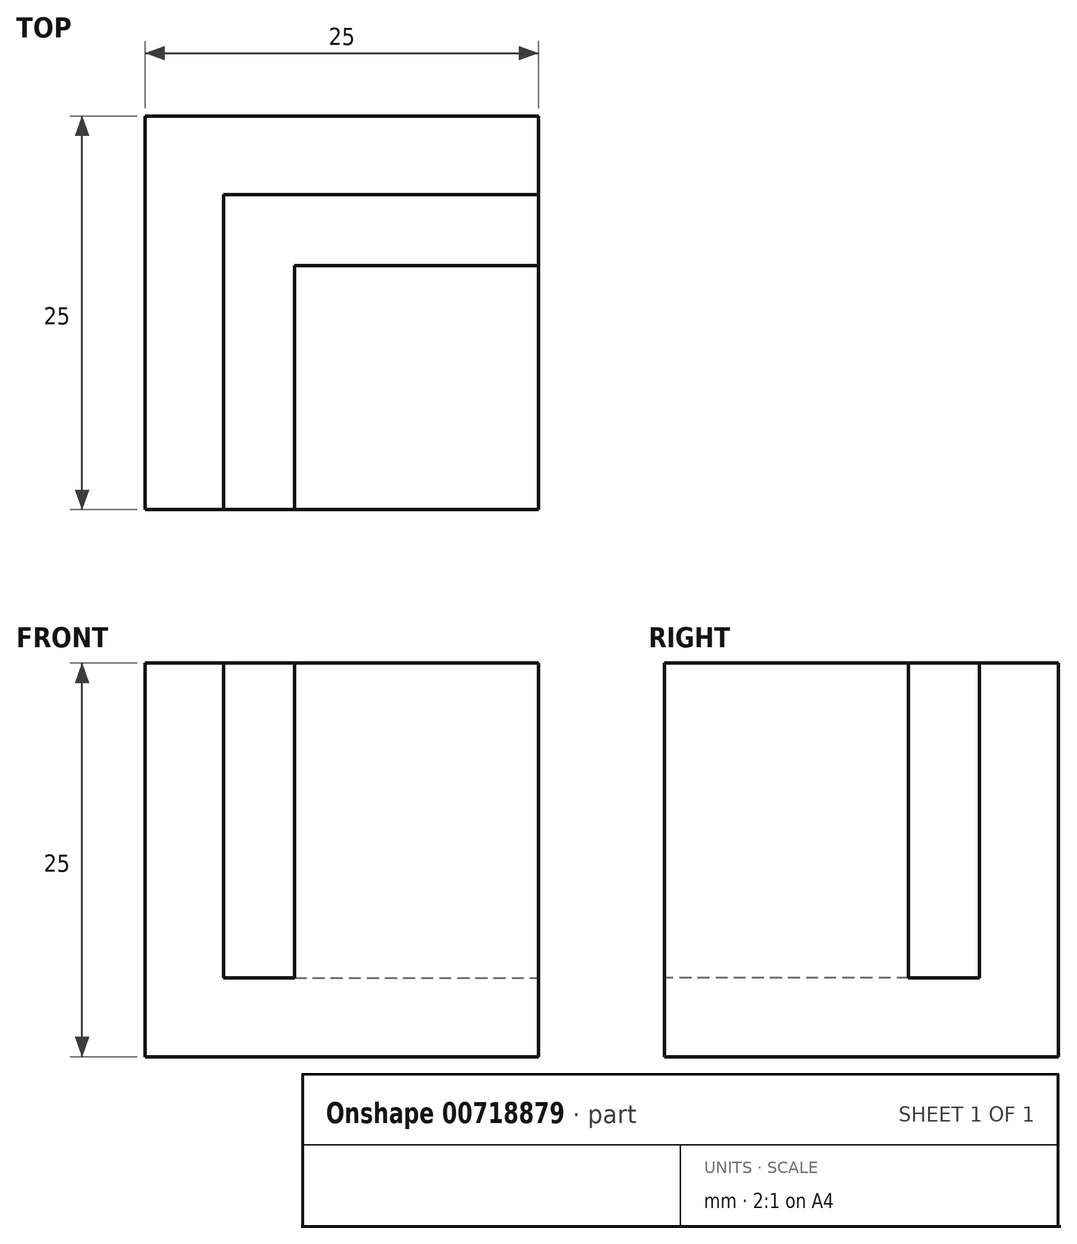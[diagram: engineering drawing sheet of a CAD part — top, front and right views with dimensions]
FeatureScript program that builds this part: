
annotation { "Feature Type Name" : "Feature", "Feature Type Description" : "" }
export const myFeature = defineFeature(function(context is Context, id is Id, definition is map)
    precondition{}
    {
        {
            var Q0;
            Q0=qCreatedBy(makeId("Top.planeOp"),FACE);
            var sketch = newSketch(context, id + "F0", { "sketchPlane" : qUnion([Q0])});
            skLineSegment(sketch, "E0.bottom", {"start": v(12.5, -12.5) * mm, "end": v(-12.5, -12.5) * mm});
            skLineSegment(sketch, "E0.top", {"start": v(12.5, 12.5) * mm, "end": v(-12.5, 12.5) * mm});
            skLineSegment(sketch, "E0.left", {"start": v(12.5, -12.5) * mm, "end": v(12.5, 12.5) * mm});
            skLineSegment(sketch, "E0.right", {"start": v(-12.5, -12.5) * mm, "end": v(-12.5, 12.5) * mm});
            skPoint(sketch, "E0.middle", {"position": v(0, 0) * mm});
            skSolve(sketch);
        }
        {
            var Q0;
            Q0 = qSketchRegion(id + "F0", true);
            extrude(context, id + "F1", {"entities" : qUnion([Q0]), "depth" : 25 * mm, "offsetDistance" : 25 * mm});
        }
        {
            var Q0;
            Q0=makeQuery(id+"F1.opExtrude","CAP_FACE",FACE,{"disambiguationData":[OSD([sQuery(id+"F0.wireOp",EDGE,"E0.bottom"),sQuery(id+"F0.wireOp",EDGE,"E0.top"),sQuery(id+"F0.wireOp",EDGE,"E0.left"),sQuery(id+"F0.wireOp",EDGE,"E0.right")])],"isStart":false});
            var sketch = newSketch(context, id + "F2", { "sketchPlane" : qUnion([Q0])});
            skLineSegment(sketch, "E1", {"start": v(-12.5, 12.5) * mm, "end": v(0, 0) * mm, "construction": true});
            skLineSegment(sketch, "E2", {"start": v(0, 12.5) * mm, "end": v(0, 7.5) * mm, "construction": true});
            skLineSegment(sketch, "E3", {"start": v(-12.5, 0) * mm, "end": v(-7.5, 0) * mm, "construction": true});
            skLineSegment(sketch, "E4.bottom", {"start": v(-7.5, 7.5) * mm, "end": v(-3, 7.5) * mm});
            skLineSegment(sketch, "E4.top", {"start": v(-7.5, -12.5) * mm, "end": v(-3, -12.5) * mm});
            skLineSegment(sketch, "E4.left", {"start": v(-7.5, 7.5) * mm, "end": v(-7.5, -12.5) * mm});
            skLineSegment(sketch, "E4.right", {"start": v(-3, 7.5) * mm, "end": v(-3, -12.5) * mm});
            skLineSegment(sketch, "E5.bottom", {"start": v(-7.5, 7.5) * mm, "end": v(12.5, 7.5) * mm});
            skLineSegment(sketch, "E5.top", {"start": v(-7.5, 3) * mm, "end": v(12.5, 3) * mm});
            skLineSegment(sketch, "E5.left", {"start": v(-7.5, 7.5) * mm, "end": v(-7.5, 3) * mm});
            skLineSegment(sketch, "E5.right", {"start": v(12.5, 7.5) * mm, "end": v(12.5, 3) * mm});
            skSolve(sketch);
        }
        {
            var Q0;
            Q0 = qSketchRegion(id + "F2", true);
            extrude(context, id + "F3", {"entities" : qUnion([Q0]), "operationType" : NewBodyOperationType.REMOVE, "oppositeDirection" : true, "depth" : 20 * mm, "offsetDistance" : 25 * mm});
        }
    });
